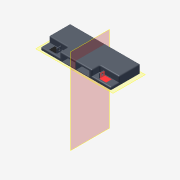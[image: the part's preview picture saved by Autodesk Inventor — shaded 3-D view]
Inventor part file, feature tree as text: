
AUTODESK INVENTOR PART (.ipt)
format: ipt  version: 2014 SP1 (Build 180222100, 222)  size: 365,568 bytes
history: native  units: mm (DEFAULTED — no unit token found)
features: sketch x10, extrude x9, fillet x5, plane x5, mirror x3, split x3, hole x1
ambient origin geometry x8: Origin, YZ Plane, XZ Plane, XY Plane, X Axis, Y Axis, Z Axis, Center Point
bodies: Solid1 (feature_tree)
feature tree (36):
  extrude  "Extrusion1"  Depth=74.422mm
  extrude  "Extrusion2"  Depth=139.7mm TaperAngle=0.0deg
  extrude  "Extrusion3"  Depth=21.336mm
  fillet  "Fillet1"  Radius=14.224mm
  fillet  "Fillet3"  Radius=2.54mm
  fillet  "Fillet4"  Radius=2.54mm
  extrude  "Extrusion4"  Depth=0.254mm TaperAngle=0.0deg
  extrude  "Extrusion5"  Depth=12.7mm TaperAngle=0.0deg
  extrude  "Extrusion6"  Depth=12.7mm TaperAngle=0.0deg
  plane  "Work Plane1"
  mirror  "Mirror1"
  mirror  "Mirror2"
  extrude  "Extrusion7"  Depth=20.32mm
  extrude  "Extrusion8"  Depth=19.558mm TaperAngle=0.0deg
  plane  "Work Plane2"
  fillet  "Fillet5"  Radius=33.02mm
  plane  "Work Plane3"
  extrude  "Extrusion9"  Depth=19.05mm TaperAngle=0.0deg
  hole  "Hole1"  [1 undecoded]
  fillet  "Fillet6"  Radius=56.261mm
  mirror  "Mirror3"
  plane  "Work Plane4"
  split  "Split2"
  plane  "Work Plane6"
  split  "Split3"
  split  "Split4"
  sketch  "Sketch1"  dims[d0=179.578mm d1=74.422mm]
  sketch  "Sketch2"  dims[d2=139.7mm d3=0.0mm d4=21.082mm d5=0.0mm]
  sketch  "Sketch3"  dims[d6=49.276mm d7=21.336mm d8=14.224mm d9=0.0mm d10=2.54mm d12=2.54mm]
  sketch  "Sketch4"  dims[d13=2.54mm d14=0.254mm d15=0.0mm]
  sketch  "Sketch5"  dims[d16=1.524mm d17=12.7mm d18=0.0mm]
  sketch  "Sketch6"  dims[d19=5.08mm d20=12.7mm d21=0.0mm]
  sketch  "Sketch7"  dims[d22=20.32mm d23=20.32mm]
  sketch  "Sketch8"  dims[d24=63.5mm d25=19.558mm d26=0.0mm d27=33.02mm]
  sketch  "Sketch9"  dims[d28=3.048mm d29=19.05mm d30=0.0mm]
  sketch  "Sketch10"  dims[d31=181.102mm d32=-127.0mm d34=1.27mm d35=56.261mm d36=11.9888mm d37=11.5062mm d38=2.0066mm d39=0.0mm d40=5.4864mm d41=5.4864mm d42=19.05mm d43=9.525mm d44=6.35mm d45=14.3117mm d46=25.4mm d47=20.594885mm d48=1.27mm d49=14.986mm d50=90.0deg d51=0.0mm]
note: 1 required parameter value undecoded (feature->parameter linkage not recoverable at this tier; creation-order binding heuristic only, values carry confidence <= 0.55)
